# Revit family: ESHL-L-480-xxx-840-PSBx
name_source: partatom
category: Leuchten
revit_build: Autodesk Revit 2017 (Build: 20190508_0315(x64)
units: mm (PartAtom-declared; Revit-internal decimal feet)

## family parameters
Basisbauteil = Fläche
Beim Laden mit Abzugskörper schneiden = Nein
Bemaßung runder Anschluss = Durchmesser verwenden
Gemeinsam genutzt = Nein
Lichtquelle = Ja
OmniClass-Nummer = 23.80.70.11
OmniClass-Titel = Luminaries for Internal Lighting
Raumberechnungspunkt = Nein
Teiletyp = Normal

## types (4) — shared parameters
Baugruppenkennzeichen = D5020200
Emissionsform beim Rendern sichtbar = Nein
Farbfilter = 16777215
Farbtemperaturverschiebung bei Dämpfen der Lampe = <Keine Auswahl>
Hersteller = RIDI Leuchten GmbH
Lampe = LED
Neigungswinkel = 90.00°
URL = www.ridi.de
Von Breite des Rechtecks ausssenden = 1496 mm  [stored 4.90814 ft]
Von Länge des Rechtecks aussenden = 568 mm  [stored 1.86352 ft]
brand = RIDI
conformity mark = CE
electrical safety class = 1
height = 85 mm  [stored 0.278871 ft]
ingress protection (IP) code = IP40
length = 1548 mm  [stored 5.07874 ft]
nominal frequency = 50-60Hz
nominal voltage = 230
voltage type (AC, DC, UC) = AC
weight = 29.75 kg
width = 624 mm  [stored 2.04724 ft]
zero-valued in all types: Vorgabe-Ansicht

## per-type parameters (varying)
| type | Datei für fotometrisches Netz | Modell | Scheinlast | rated input power |
| ESHL-L 480/2680-840 PSB | ESHL-L 4802680-840 PSB.IES | 0850175 | 192 VA | 192 |
| ESHL-L 480/2680-840 PSB-DA | ESHL-L 4802680-840 PSB.IES | 0860175 | 192 VA | 192 |
| ESHL-L 480/3360-840 PSB | ESHL-L 4803360-840 PSB.IES | 0850617 | 244 VA | 244 |
| ESHL-L 480/3360-840 PSB-DA | ESHL-L 4803360-840 PSB.IES | 0860617 | 244 VA | 244 |

note: column(s) folded — value = type name in every type: product name

note: [stored X ft] marks values corroborated as IEEE doubles in the binary element streams (Revit-internal decimal feet)
